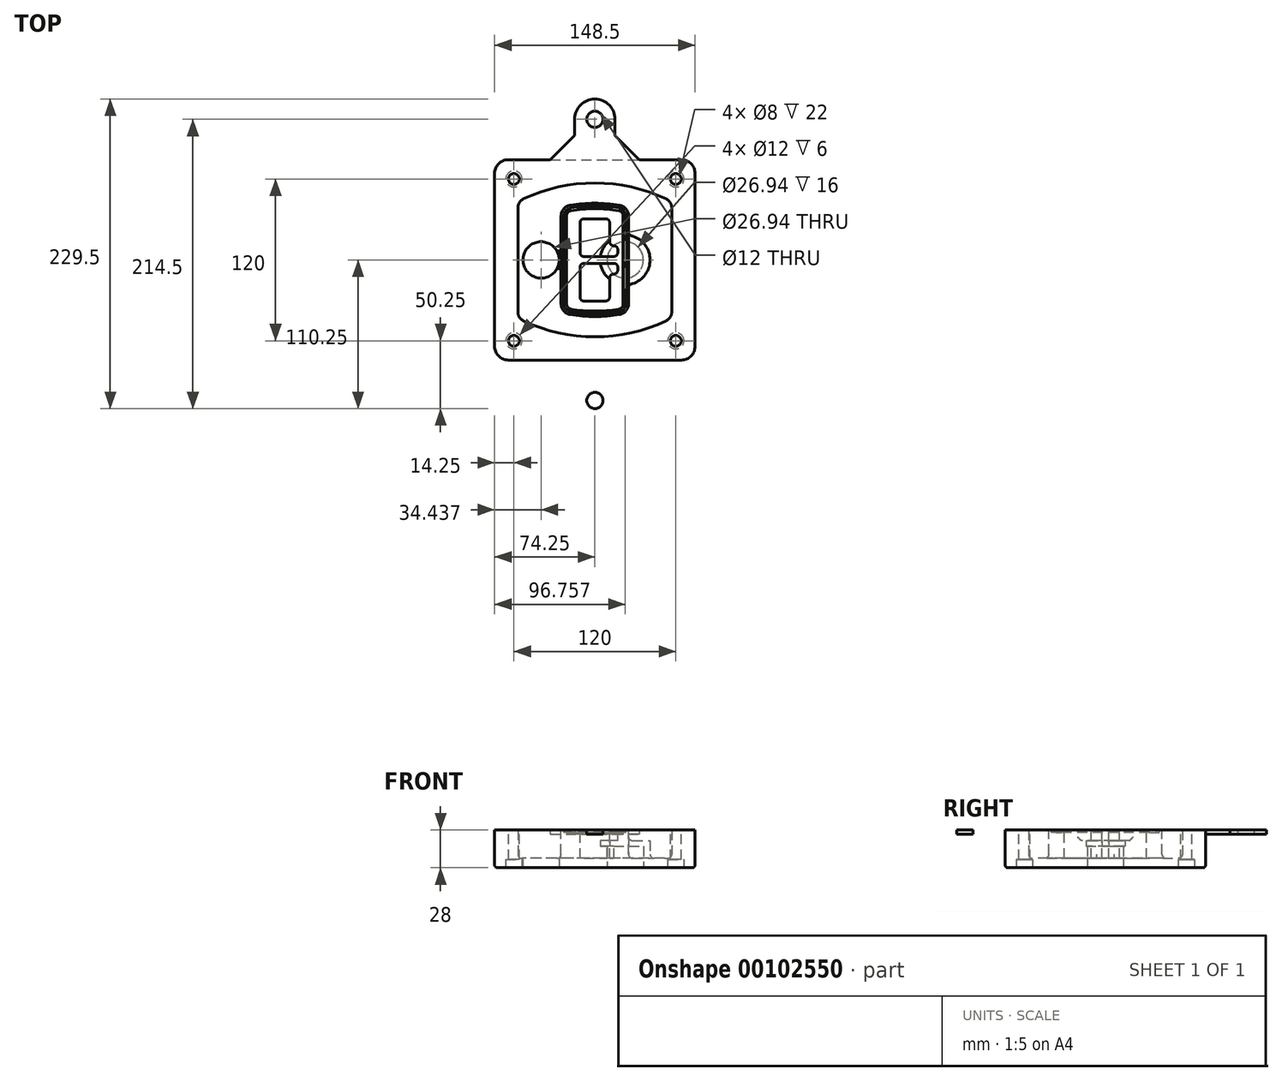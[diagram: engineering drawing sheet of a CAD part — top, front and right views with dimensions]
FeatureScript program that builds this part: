
annotation { "Feature Type Name" : "Feature", "Feature Type Description" : "" }
export const myFeature = defineFeature(function(context is Context, id is Id, definition is map)
    precondition{}
    {
        {
            var Q0;
            Q0=qCreatedBy(makeId("Top.planeOp"),FACE);
            var sketch = newSketch(context, id + "F0", { "sketchPlane" : qUnion([Q0])});
            skPoint(sketch, "E0.rect.middle", {"position": v(0, 0) * mm});
            skLineSegment(sketch, "E1.bottom", {"start": v(-64.25, -74.25) * mm, "end": v(64.25, -74.25) * mm});
            skLineSegment(sketch, "E1.top", {"start": v(-64.25, 74.25) * mm, "end": v(64.25, 74.25) * mm});
            skLineSegment(sketch, "E1.left", {"start": v(-74.25, -64.25) * mm, "end": v(-74.25, 64.25) * mm});
            skLineSegment(sketch, "E1.right", {"start": v(74.25, -64.25) * mm, "end": v(74.25, 64.25) * mm});
            skLineSegment(sketch, "E2", {"start": v(-74.25, 74.25) * mm, "end": v(74.25, -74.25) * mm, "construction": true});
            skLineSegment(sketch, "E3", {"start": v(74.25, 74.25) * mm, "end": v(-74.25, -74.25) * mm, "construction": true});
            skCircle(sketch, "E4", {"center": v(-60, 60) * mm, "radius": 4 * mm});
            skCircle(sketch, "E5", {"center": v(60, 60) * mm, "radius": 4 * mm});
            skCircle(sketch, "E6", {"center": v(60, -60) * mm, "radius": 4 * mm});
            skCircle(sketch, "E7", {"center": v(-60, -60) * mm, "radius": 4 * mm});
            skLineSegment(sketch, "E8", {"start": v(-60, 60) * mm, "end": v(60, 60) * mm, "construction": true});
            skLineSegment(sketch, "E9", {"start": v(60, 60) * mm, "end": v(60, -60) * mm, "construction": true});
            skLineSegment(sketch, "E10", {"start": v(60, -60) * mm, "end": v(-60, -60) * mm, "construction": true});
            skLineSegment(sketch, "E11", {"start": v(-60, -60) * mm, "end": v(-60, 60) * mm, "construction": true});
            skLineSegment(sketch, "E12", {"start": v(-60, 38.83) * mm, "end": v(-60, -38.83) * mm});
            skLineSegment(sketch, "E13", {"start": v(60, 38.83) * mm, "end": v(60, -38.83) * mm});
            skArc(sketch, "E14", {"start": v(54.26, 47.88) * mm, "mid": v(0, 60) * mm, "end": v(-54.26, 47.88) * mm});
            skArc(sketch, "E15", {"start": v(-54.26, -47.88) * mm, "mid": v(0, -60) * mm, "end": v(54.26, -47.88) * mm});
            skLineSegment(sketch, "E16", {"start": v(-60, 0) * mm, "end": v(60, 0) * mm, "construction": true});
            skPoint(sketch, "E17.visualSharp", {"position": v(-60, -45) * mm});
            skArc(sketch, "E17.filletArc", {"start": v(-60, -38.83) * mm, "mid": v(-58.44, -44.2) * mm, "end": v(-54.26, -47.88) * mm});
            skPoint(sketch, "E18.visualSharp", {"position": v(-60, 45) * mm});
            skArc(sketch, "E18.filletArc", {"start": v(-54.26, 47.88) * mm, "mid": v(-58.44, 44.2) * mm, "end": v(-60, 38.83) * mm});
            skPoint(sketch, "E19.visualSharp", {"position": v(60, 45) * mm});
            skArc(sketch, "E19.filletArc", {"start": v(60, 38.83) * mm, "mid": v(58.44, 44.2) * mm, "end": v(54.26, 47.88) * mm});
            skPoint(sketch, "E20.visualSharp", {"position": v(60, -45) * mm});
            skArc(sketch, "E20.filletArc", {"start": v(54.26, -47.88) * mm, "mid": v(58.44, -44.2) * mm, "end": v(60, -38.83) * mm});
            skPoint(sketch, "E21.visualSharp", {"position": v(-74.25, 74.25) * mm});
            skArc(sketch, "E21.filletArc", {"start": v(-64.25, 74.25) * mm, "mid": v(-71.32, 71.32) * mm, "end": v(-74.25, 64.25) * mm});
            skPoint(sketch, "E22.visualSharp", {"position": v(74.25, 74.25) * mm});
            skArc(sketch, "E22.filletArc", {"start": v(74.25, 64.25) * mm, "mid": v(71.32, 71.32) * mm, "end": v(64.25, 74.25) * mm});
            skPoint(sketch, "E23.visualSharp", {"position": v(74.25, -74.25) * mm});
            skArc(sketch, "E23.filletArc", {"start": v(64.25, -74.25) * mm, "mid": v(71.32, -71.32) * mm, "end": v(74.25, -64.25) * mm});
            skPoint(sketch, "E24.visualSharp", {"position": v(-74.25, -74.25) * mm});
            skArc(sketch, "E24.filletArc", {"start": v(-74.25, -64.25) * mm, "mid": v(-71.32, -71.32) * mm, "end": v(-64.25, -74.25) * mm});
            skArc(sketch, "E25.0", {"start": v(57, 38.83) * mm, "mid": v(55.9, 42.58) * mm, "end": v(52.98, 45.17) * mm});
            skLineSegment(sketch, "E25.1", {"start": v(57, 38.83) * mm, "end": v(57, -38.83) * mm});
            skArc(sketch, "E25.2", {"start": v(52.98, -45.17) * mm, "mid": v(55.9, -42.58) * mm, "end": v(57, -38.83) * mm});
            skArc(sketch, "E25.3", {"start": v(-52.98, -45.17) * mm, "mid": v(0, -57) * mm, "end": v(52.98, -45.17) * mm});
            skArc(sketch, "E25.4", {"start": v(-57, -38.83) * mm, "mid": v(-55.9, -42.58) * mm, "end": v(-52.98, -45.17) * mm});
            skArc(sketch, "E25.5", {"start": v(52.98, 45.17) * mm, "mid": v(0, 57) * mm, "end": v(-52.98, 45.17) * mm});
            skLineSegment(sketch, "E25.6", {"start": v(-57, 38.83) * mm, "end": v(-57, -38.83) * mm});
            skArc(sketch, "E25.7", {"start": v(-52.98, 45.17) * mm, "mid": v(-55.9, 42.58) * mm, "end": v(-57, 38.83) * mm});
            skArc(sketch, "E26.0", {"start": v(-55.96, 51.5) * mm, "mid": v(-61.82, 46.33) * mm, "end": v(-64, 38.83) * mm});
            skArc(sketch, "E26.1", {"start": v(55.96, 51.5) * mm, "mid": v(0, 64) * mm, "end": v(-55.96, 51.5) * mm});
            skArc(sketch, "E26.2", {"start": v(64, 38.83) * mm, "mid": v(61.82, 46.33) * mm, "end": v(55.96, 51.5) * mm});
            skLineSegment(sketch, "E26.3", {"start": v(64, 38.83) * mm, "end": v(64, -38.83) * mm});
            skArc(sketch, "E26.4", {"start": v(55.96, -51.5) * mm, "mid": v(61.82, -46.33) * mm, "end": v(64, -38.83) * mm});
            skLineSegment(sketch, "E26.5", {"start": v(-64, 38.83) * mm, "end": v(-64, -38.83) * mm});
            skArc(sketch, "E26.6", {"start": v(-55.96, -51.5) * mm, "mid": v(0, -64) * mm, "end": v(55.96, -51.5) * mm});
            skArc(sketch, "E26.7", {"start": v(-64, -38.83) * mm, "mid": v(-61.82, -46.33) * mm, "end": v(-55.96, -51.5) * mm});
            skSolve(sketch);
        }
        {
            var Q0;
            Q0=makeQuery(id+"F0.imprint","IMPRINT",FACE,{"disambiguationData":[TD([[makeQuery(id+"F0.imprint","IMPRINT",EDGE,{"derivedFrom":sQuery(id+"F0.wireOp",EDGE,"E1.bottom")}),1.0]])]});
            var Q1;
            Q1=makeQuery(id+"F0.imprint","IMPRINT",FACE,{"disambiguationData":[TD([[makeQuery(id+"F0.imprint","IMPRINT",EDGE,{"derivedFrom":sQuery(id+"F0.wireOp",EDGE,"E12")}),1.0]])]});
            var Q2;
            Q2=makeQuery(id+"F0.imprint","IMPRINT",FACE,{"disambiguationData":[TD([[makeQuery(id+"F0.imprint","IMPRINT",EDGE,{"derivedFrom":sQuery(id+"F0.wireOp",EDGE,"E25.0")}),1.0]])]});
            var Q3;
            Q3=makeQuery(id+"F0.imprint","IMPRINT",FACE,{"disambiguationData":[TD([[makeQuery(id+"F0.imprint","IMPRINT",EDGE,{"derivedFrom":sQuery(id+"F0.wireOp",EDGE,"E12")}),-1.0]])]});
            extrude(context, id + "F1", {"entities" : qUnion([Q0, Q1, Q2, Q3]), "oppositeDirection" : true, "depth" : 25 * mm});
        }
        {
            var Q0;
            Q0=makeQuery(id+"F0.imprint","IMPRINT",FACE,{"disambiguationData":[TD([[makeQuery(id+"F0.imprint","IMPRINT",EDGE,{"derivedFrom":sQuery(id+"F0.wireOp",EDGE,"E12")}),1.0]])]});
            extrude(context, id + "F2", {"entities" : qUnion([Q0]), "operationType" : NewBodyOperationType.ADD, "depth" : 3 * mm});
        }
        {
            var Q0;
            Q0=makeQuery(id+"F0.imprint","IMPRINT",FACE,{"disambiguationData":[TD([[makeQuery(id+"F0.imprint","IMPRINT",EDGE,{"derivedFrom":sQuery(id+"F0.wireOp",EDGE,"E25.0")}),1.0]])]});
            extrude(context, id + "F3", {"entities" : qUnion([Q0]), "operationType" : NewBodyOperationType.REMOVE, "oppositeDirection" : true, "depth" : 18 * mm});
        }
        {
            var Q0;
            Q0=makeQuery(id+"F2.opExtrude","CAP_FACE",FACE,{"disambiguationData":[OSD([sQuery(id+"F0.wireOp",EDGE,"E12"),sQuery(id+"F0.wireOp",EDGE,"E13"),sQuery(id+"F0.wireOp",EDGE,"E14"),sQuery(id+"F0.wireOp",EDGE,"E15"),sQuery(id+"F0.wireOp",EDGE,"E17.filletArc"),sQuery(id+"F0.wireOp",EDGE,"E18.filletArc"),sQuery(id+"F0.wireOp",EDGE,"E19.filletArc"),sQuery(id+"F0.wireOp",EDGE,"E20.filletArc"),sQuery(id+"F0.wireOp",EDGE,"E25.0"),sQuery(id+"F0.wireOp",EDGE,"E25.1"),sQuery(id+"F0.wireOp",EDGE,"E25.2"),sQuery(id+"F0.wireOp",EDGE,"E25.3"),sQuery(id+"F0.wireOp",EDGE,"E25.4"),sQuery(id+"F0.wireOp",EDGE,"E25.5"),sQuery(id+"F0.wireOp",EDGE,"E25.6"),sQuery(id+"F0.wireOp",EDGE,"E25.7")])],"isStart":false});
            var sketch = newSketch(context, id + "F4", { "sketchPlane" : qUnion([Q0])});
            skArc(sketch, "E27.0", {"start": v(-18.34, -40.45) * mm, "mid": v(0, -42) * mm, "end": v(18.34, -40.45) * mm});
            skArc(sketch, "E28.0", {"start": v(18.34, 40.45) * mm, "mid": v(0, 42) * mm, "end": v(-18.34, 40.45) * mm});
            skLineSegment(sketch, "E29", {"start": v(-25, 32.57) * mm, "end": v(-25, -32.57) * mm});
            skLineSegment(sketch, "E30", {"start": v(25, 32.57) * mm, "end": v(25, -32.57) * mm});
            skLineSegment(sketch, "E31", {"start": v(-25, 39.1) * mm, "end": v(25, 39.1) * mm, "construction": true});
            skLineSegment(sketch, "E32", {"start": v(-25, -39.1) * mm, "end": v(25, -39.1) * mm, "construction": true});
            skPoint(sketch, "E33.visualSharp", {"position": v(-25, 39.1) * mm});
            skArc(sketch, "E33.filletArc", {"start": v(-18.34, 40.45) * mm, "mid": v(-23.11, 37.73) * mm, "end": v(-25, 32.57) * mm});
            skPoint(sketch, "E34.visualSharp", {"position": v(25, 39.1) * mm});
            skArc(sketch, "E34.filletArc", {"start": v(25, 32.57) * mm, "mid": v(23.11, 37.73) * mm, "end": v(18.34, 40.45) * mm});
            skPoint(sketch, "E35.visualSharp", {"position": v(25, -39.1) * mm});
            skArc(sketch, "E35.filletArc", {"start": v(18.34, -40.45) * mm, "mid": v(23.11, -37.73) * mm, "end": v(25, -32.57) * mm});
            skPoint(sketch, "E36.visualSharp", {"position": v(-25, -39.1) * mm});
            skArc(sketch, "E36.filletArc", {"start": v(-25, -32.57) * mm, "mid": v(-23.11, -37.73) * mm, "end": v(-18.34, -40.45) * mm});
            skArc(sketch, "E37.0", {"start": v(52.98, 45.17) * mm, "mid": v(0, 57) * mm, "end": v(-52.98, 45.17) * mm});
            skArc(sketch, "E37.1", {"start": v(-52.98, 45.17) * mm, "mid": v(-55.9, 42.58) * mm, "end": v(-57, 38.83) * mm});
            skLineSegment(sketch, "E37.2", {"start": v(-57, 38.83) * mm, "end": v(-57, -38.83) * mm});
            skArc(sketch, "E37.3", {"start": v(-57, -38.83) * mm, "mid": v(-55.9, -42.58) * mm, "end": v(-52.98, -45.17) * mm});
            skArc(sketch, "E37.4", {"start": v(-52.98, -45.17) * mm, "mid": v(0, -57) * mm, "end": v(52.98, -45.17) * mm});
            skArc(sketch, "E37.5", {"start": v(52.98, -45.17) * mm, "mid": v(55.9, -42.58) * mm, "end": v(57, -38.83) * mm});
            skLineSegment(sketch, "E37.6", {"start": v(57, 38.83) * mm, "end": v(57, -38.83) * mm});
            skArc(sketch, "E37.7", {"start": v(57, 38.83) * mm, "mid": v(55.9, 42.58) * mm, "end": v(52.98, 45.17) * mm});
            skLineSegment(sketch, "E38.0", {"start": v(23, 32.57) * mm, "end": v(23, -32.57) * mm});
            skArc(sketch, "E38.1", {"start": v(18, -38.48) * mm, "mid": v(21.58, -36.44) * mm, "end": v(23, -32.57) * mm});
            skArc(sketch, "E38.2", {"start": v(-18, -38.48) * mm, "mid": v(0, -40) * mm, "end": v(18, -38.48) * mm});
            skArc(sketch, "E38.3", {"start": v(-23, -32.57) * mm, "mid": v(-21.58, -36.44) * mm, "end": v(-18, -38.48) * mm});
            skLineSegment(sketch, "E38.4", {"start": v(-23, 32.57) * mm, "end": v(-23, -32.57) * mm});
            skArc(sketch, "E38.5", {"start": v(23, 32.57) * mm, "mid": v(21.58, 36.44) * mm, "end": v(18, 38.48) * mm});
            skArc(sketch, "E38.6", {"start": v(-18, 38.48) * mm, "mid": v(-21.58, 36.44) * mm, "end": v(-23, 32.57) * mm});
            skArc(sketch, "E38.7", {"start": v(18, 38.48) * mm, "mid": v(0, 40) * mm, "end": v(-18, 38.48) * mm});
            skArc(sketch, "E39.0", {"start": v(21, 32.57) * mm, "mid": v(20.06, 35.15) * mm, "end": v(17.67, 36.5) * mm});
            skLineSegment(sketch, "E39.1", {"start": v(21, 32.57) * mm, "end": v(21, -32.57) * mm});
            skArc(sketch, "E39.2", {"start": v(17.67, -36.5) * mm, "mid": v(20.06, -35.15) * mm, "end": v(21, -32.57) * mm});
            skArc(sketch, "E39.3", {"start": v(-17.67, -36.5) * mm, "mid": v(0, -38) * mm, "end": v(17.67, -36.5) * mm});
            skArc(sketch, "E39.4", {"start": v(-21, -32.57) * mm, "mid": v(-20.06, -35.15) * mm, "end": v(-17.67, -36.5) * mm});
            skArc(sketch, "E39.5", {"start": v(17.67, 36.5) * mm, "mid": v(0, 38) * mm, "end": v(-17.67, 36.5) * mm});
            skLineSegment(sketch, "E39.6", {"start": v(-21, 32.57) * mm, "end": v(-21, -32.57) * mm});
            skArc(sketch, "E39.7", {"start": v(-17.67, 36.5) * mm, "mid": v(-20.06, 35.15) * mm, "end": v(-21, 32.57) * mm});
            skLineSegment(sketch, "E40", {"start": v(-25, 0) * mm, "end": v(25, 0) * mm, "construction": true});
            skLineSegment(sketch, "E41", {"start": v(-11, 5.5) * mm, "end": v(-11, 27.5) * mm});
            skLineSegment(sketch, "E42", {"start": v(-8, 30.5) * mm, "end": v(8, 30.5) * mm});
            skLineSegment(sketch, "E43", {"start": v(11, 27.5) * mm, "end": v(11, 13.5) * mm});
            skLineSegment(sketch, "E44", {"start": v(14, 10.5) * mm, "end": v(14, 10.5) * mm});
            skLineSegment(sketch, "E45", {"start": v(17, 7.5) * mm, "end": v(17, 5.5) * mm});
            skLineSegment(sketch, "E46", {"start": v(14, 2.5) * mm, "end": v(-8, 2.5) * mm});
            skPoint(sketch, "E47.visualSharp", {"position": v(-11, 30.5) * mm});
            skArc(sketch, "E47.filletArc", {"start": v(-8, 30.5) * mm, "mid": v(-10.12, 29.62) * mm, "end": v(-11, 27.5) * mm});
            skPoint(sketch, "E48.visualSharp", {"position": v(11, 30.5) * mm});
            skArc(sketch, "E48.filletArc", {"start": v(11, 27.5) * mm, "mid": v(10.12, 29.62) * mm, "end": v(8, 30.5) * mm});
            skPoint(sketch, "E49.visualSharp", {"position": v(11, 10.5) * mm});
            skArc(sketch, "E49.filletArc", {"start": v(11, 13.5) * mm, "mid": v(11.88, 11.38) * mm, "end": v(14, 10.5) * mm});
            skPoint(sketch, "E50.visualSharp", {"position": v(17, 10.5) * mm});
            skArc(sketch, "E50.filletArc", {"start": v(17, 7.5) * mm, "mid": v(16.12, 9.62) * mm, "end": v(14, 10.5) * mm});
            skPoint(sketch, "E51.visualSharp", {"position": v(17, 2.5) * mm});
            skArc(sketch, "E51.filletArc", {"start": v(14, 2.5) * mm, "mid": v(16.12, 3.38) * mm, "end": v(17, 5.5) * mm});
            skPoint(sketch, "E52.visualSharp", {"position": v(-11, 2.5) * mm});
            skArc(sketch, "E52.filletArc", {"start": v(-11, 5.5) * mm, "mid": v(-10.12, 3.38) * mm, "end": v(-8, 2.5) * mm});
            skLineSegment(sketch, "E53.0.MirrorCS", {"start": v(14, -2.5) * mm, "end": v(-8, -2.5) * mm});
            skArc(sketch, "E54.0.MirrorCS", {"start": v(-11, -5.5) * mm, "mid": v(-10.12, -3.38) * mm, "end": v(-8, -2.5) * mm});
            skLineSegment(sketch, "E55.0.MirrorCS", {"start": v(-11, -5.5) * mm, "end": v(-11, -27.5) * mm});
            skArc(sketch, "E56.0.MirrorCS", {"start": v(-8, -30.5) * mm, "mid": v(-10.12, -29.62) * mm, "end": v(-11, -27.5) * mm});
            skLineSegment(sketch, "E57.0.MirrorCS", {"start": v(-8, -30.5) * mm, "end": v(8, -30.5) * mm});
            skArc(sketch, "E58.0.MirrorCS", {"start": v(11, -27.5) * mm, "mid": v(10.12, -29.62) * mm, "end": v(8, -30.5) * mm});
            skLineSegment(sketch, "E59.0.MirrorCS", {"start": v(11, -27.5) * mm, "end": v(11, -13.5) * mm});
            skArc(sketch, "E60.0.MirrorCS", {"start": v(11, -13.5) * mm, "mid": v(11.88, -11.38) * mm, "end": v(14, -10.5) * mm});
            skArc(sketch, "E61.0.MirrorCS", {"start": v(17, -7.5) * mm, "mid": v(16.12, -9.62) * mm, "end": v(14, -10.5) * mm});
            skLineSegment(sketch, "E62.0.MirrorCS", {"start": v(17, -7.5) * mm, "end": v(17, -5.5) * mm});
            skArc(sketch, "E63.0.MirrorCS", {"start": v(14, -2.5) * mm, "mid": v(16.12, -3.38) * mm, "end": v(17, -5.5) * mm});
            skSolve(sketch);
        }
        {
            var Q0;
            Q0=makeQuery(id+"F4.imprint","IMPRINT",FACE,{"disambiguationData":[TD([[makeQuery(id+"F4.imprint","IMPRINT",EDGE,{"derivedFrom":sQuery(id+"F4.wireOp",EDGE,"E27.0")}),1.0]])]});
            var Q1;
            Q1=makeQuery(id+"F4.imprint","IMPRINT",FACE,{"disambiguationData":[TD([[makeQuery(id+"F4.imprint","IMPRINT",EDGE,{"derivedFrom":sQuery(id+"F4.wireOp",EDGE,"E38.0")}),-1.0]])]});
            var Q2;
            Q2=makeQuery(id+"F4.imprint","IMPRINT",FACE,{"disambiguationData":[TD([[makeQuery(id+"F4.imprint","IMPRINT",EDGE,{"derivedFrom":sQuery(id+"F4.wireOp",EDGE,"E39.0")}),1.0]])]});
            extrude(context, id + "F5", {"entities" : qUnion([Q0, Q1, Q2]), "operationType" : NewBodyOperationType.ADD, "endBound" : BoundingType.UP_TO_NEXT, "oppositeDirection" : true, "depth" : 25 * mm});
        }
        {
            var Q0;
            Q0=makeQuery(id+"F4.imprint","IMPRINT",FACE,{"disambiguationData":[TD([[makeQuery(id+"F4.imprint","IMPRINT",EDGE,{"derivedFrom":sQuery(id+"F4.wireOp",EDGE,"E38.0")}),-1.0]])]});
            extrude(context, id + "F6", {"entities" : qUnion([Q0]), "operationType" : NewBodyOperationType.REMOVE, "oppositeDirection" : true, "depth" : 2 * mm});
        }
        {
            var Q0;
            Q0=makeQuery(id+"F1.opExtrude","CAP_FACE",FACE,{"disambiguationData":[OSD([sQuery(id+"F0.wireOp",EDGE,"E1.bottom"),sQuery(id+"F0.wireOp",EDGE,"E1.top"),sQuery(id+"F0.wireOp",EDGE,"E1.left"),sQuery(id+"F0.wireOp",EDGE,"E1.right"),sQuery(id+"F0.wireOp",EDGE,"E4"),sQuery(id+"F0.wireOp",EDGE,"E5"),sQuery(id+"F0.wireOp",EDGE,"E6"),sQuery(id+"F0.wireOp",EDGE,"E7"),sQuery(id+"F0.wireOp",EDGE,"E21.filletArc"),sQuery(id+"F0.wireOp",EDGE,"E22.filletArc"),sQuery(id+"F0.wireOp",EDGE,"E23.filletArc"),sQuery(id+"F0.wireOp",EDGE,"E24.filletArc")])],"isStart":false});
            var sketch = newSketch(context, id + "F7", { "sketchPlane" : qUnion([Q0])});
            skCircle(sketch, "E64", {"center": v(22.5, 0) * mm, "radius": 13.47 * mm});
            skCircle(sketch, "E65", {"center": v(-39.81, 0) * mm, "radius": 13.47 * mm});
            skLineSegment(sketch, "E66", {"start": v(74.25, 0) * mm, "end": v(-74.25, 0) * mm});
            skCircle(sketch, "E67", {"center": v(22.5, 0) * mm, "radius": 18.47 * mm});
            skCircle(sketch, "E68", {"center": v(60, -60) * mm, "radius": 6 * mm});
            skCircle(sketch, "E69", {"center": v(-60, -60) * mm, "radius": 6 * mm});
            skCircle(sketch, "E70", {"center": v(-60, 60) * mm, "radius": 6 * mm});
            skCircle(sketch, "E71", {"center": v(60, 60) * mm, "radius": 6 * mm});
            skSolve(sketch);
        }
        {
            var Q0;
            {var subQ1=sQuery(id+"F7.wireOp",EDGE,"E66");var subQ4=sQuery(id+"F7.wireOp",EDGE,"E64");var subQ6=makeQuery(id+"F7.imprint","INTERSECT",VERTEX,{"disambiguationData":[OD(0.0)],"derivedFrom":[subQ4,subQ1]});Q0=makeQuery(id+"F7.imprint","IMPRINT",FACE,{"disambiguationData":[TD([[makeQuery(id+"F7.imprint","IMPRINT",EDGE,{"disambiguationData":[TD([[subQ6,-1.0]])],"derivedFrom":subQ4}),-1.0]])]});}
            var Q1;
            {var subQ0=sQuery(id+"F7.wireOp",EDGE,"E66");var subQ1=sQuery(id+"F7.wireOp",EDGE,"E64");var subQ3=makeQuery(id+"F7.imprint","INTERSECT",VERTEX,{"disambiguationData":[OD(0.0)],"derivedFrom":[subQ1,subQ0]});Q1=makeQuery(id+"F7.imprint","IMPRINT",FACE,{"disambiguationData":[TD([[makeQuery(id+"F7.imprint","IMPRINT",EDGE,{"disambiguationData":[TD([[subQ3,-1.0]])],"derivedFrom":subQ1}),1.0]])]});}
            var Q2;
            {var subQ0=sQuery(id+"F7.wireOp",EDGE,"E66");var subQ1=sQuery(id+"F7.wireOp",EDGE,"E64");var subQ3=makeQuery(id+"F7.imprint","INTERSECT",VERTEX,{"disambiguationData":[OD(0.0)],"derivedFrom":[subQ1,subQ0]});Q2=makeQuery(id+"F7.imprint","IMPRINT",FACE,{"disambiguationData":[TD([[makeQuery(id+"F7.imprint","IMPRINT",EDGE,{"disambiguationData":[TD([[subQ3,1.0]])],"derivedFrom":subQ1}),1.0]])]});}
            var Q3;
            {var subQ1=sQuery(id+"F7.wireOp",EDGE,"E66");var subQ4=sQuery(id+"F7.wireOp",EDGE,"E64");var subQ6=makeQuery(id+"F7.imprint","INTERSECT",VERTEX,{"disambiguationData":[OD(0.0)],"derivedFrom":[subQ4,subQ1]});Q3=makeQuery(id+"F7.imprint","IMPRINT",FACE,{"disambiguationData":[TD([[makeQuery(id+"F7.imprint","IMPRINT",EDGE,{"disambiguationData":[TD([[subQ6,1.0]])],"derivedFrom":subQ4}),-1.0]])]});}
            extrude(context, id + "F8", {"entities" : qUnion([Q0, Q1, Q2, Q3]), "operationType" : NewBodyOperationType.ADD, "oppositeDirection" : true, "depth" : 20 * mm});
        }
        {
            var Q0;
            {var subQ0=sQuery(id+"F7.wireOp",EDGE,"E66");var subQ1=sQuery(id+"F7.wireOp",EDGE,"E64");var subQ3=makeQuery(id+"F7.imprint","INTERSECT",VERTEX,{"disambiguationData":[OD(0.0)],"derivedFrom":[subQ1,subQ0]});Q0=makeQuery(id+"F7.imprint","IMPRINT",FACE,{"disambiguationData":[TD([[makeQuery(id+"F7.imprint","IMPRINT",EDGE,{"disambiguationData":[TD([[subQ3,-1.0]])],"derivedFrom":subQ1}),1.0]])]});}
            var Q1;
            {var subQ0=sQuery(id+"F7.wireOp",EDGE,"E66");var subQ1=sQuery(id+"F7.wireOp",EDGE,"E64");var subQ3=makeQuery(id+"F7.imprint","INTERSECT",VERTEX,{"disambiguationData":[OD(0.0)],"derivedFrom":[subQ1,subQ0]});Q1=makeQuery(id+"F7.imprint","IMPRINT",FACE,{"disambiguationData":[TD([[makeQuery(id+"F7.imprint","IMPRINT",EDGE,{"disambiguationData":[TD([[subQ3,1.0]])],"derivedFrom":subQ1}),1.0]])]});}
            extrude(context, id + "F9", {"entities" : qUnion([Q0, Q1]), "operationType" : NewBodyOperationType.REMOVE, "oppositeDirection" : true, "depth" : 16 * mm});
        }
        {
            var Q0;
            {var subQ0=sQuery(id+"F7.wireOp",EDGE,"E66");var subQ1=sQuery(id+"F7.wireOp",EDGE,"E65");var subQ3=makeQuery(id+"F7.imprint","INTERSECT",VERTEX,{"disambiguationData":[OD(0.0)],"derivedFrom":[subQ1,subQ0]});Q0=makeQuery(id+"F7.imprint","IMPRINT",FACE,{"disambiguationData":[TD([[makeQuery(id+"F7.imprint","IMPRINT",EDGE,{"disambiguationData":[TD([[subQ3,-1.0]])],"derivedFrom":subQ1}),1.0]])]});}
            var Q1;
            {var subQ0=sQuery(id+"F7.wireOp",EDGE,"E66");var subQ1=sQuery(id+"F7.wireOp",EDGE,"E65");var subQ3=makeQuery(id+"F7.imprint","INTERSECT",VERTEX,{"disambiguationData":[OD(0.0)],"derivedFrom":[subQ1,subQ0]});Q1=makeQuery(id+"F7.imprint","IMPRINT",FACE,{"disambiguationData":[TD([[makeQuery(id+"F7.imprint","IMPRINT",EDGE,{"disambiguationData":[TD([[subQ3,1.0]])],"derivedFrom":subQ1}),1.0]])]});}
            extrude(context, id + "F10", {"entities" : qUnion([Q0, Q1]), "operationType" : NewBodyOperationType.REMOVE, "oppositeDirection" : true, "depth" : 25 * mm});
        }
        {
            var Q0;
            Q0=makeQuery(id+"F7.imprint","IMPRINT",FACE,{"disambiguationData":[TD([[makeQuery(id+"F7.imprint","IMPRINT",EDGE,{"derivedFrom":sQuery(id+"F7.wireOp",EDGE,"E68")}),1.0]])]});
            var Q1;
            Q1=makeQuery(id+"F7.imprint","IMPRINT",FACE,{"disambiguationData":[TD([[makeQuery(id+"F7.imprint","IMPRINT",EDGE,{"derivedFrom":makeQuery(id+"F1.opExtrude","CAP_EDGE",EDGE,{"disambiguationData":[OSD([sQuery(id+"F0.wireOp",EDGE,"E5")])],"isStart":false})}),-1.0]])]});
            var Q2;
            Q2=makeQuery(id+"F7.imprint","IMPRINT",FACE,{"disambiguationData":[TD([[makeQuery(id+"F7.imprint","IMPRINT",EDGE,{"derivedFrom":sQuery(id+"F7.wireOp",EDGE,"E69")}),1.0]])]});
            var Q3;
            Q3=makeQuery(id+"F7.imprint","IMPRINT",FACE,{"disambiguationData":[TD([[makeQuery(id+"F7.imprint","IMPRINT",EDGE,{"derivedFrom":makeQuery(id+"F1.opExtrude","CAP_EDGE",EDGE,{"disambiguationData":[OSD([sQuery(id+"F0.wireOp",EDGE,"E4")])],"isStart":false})}),-1.0]])]});
            var Q4;
            Q4=makeQuery(id+"F7.imprint","IMPRINT",FACE,{"disambiguationData":[TD([[makeQuery(id+"F7.imprint","IMPRINT",EDGE,{"derivedFrom":sQuery(id+"F7.wireOp",EDGE,"E70")}),1.0]])]});
            var Q5;
            Q5=makeQuery(id+"F7.imprint","IMPRINT",FACE,{"disambiguationData":[TD([[makeQuery(id+"F7.imprint","IMPRINT",EDGE,{"derivedFrom":makeQuery(id+"F1.opExtrude","CAP_EDGE",EDGE,{"disambiguationData":[OSD([sQuery(id+"F0.wireOp",EDGE,"E7")])],"isStart":false})}),-1.0]])]});
            var Q6;
            Q6=makeQuery(id+"F7.imprint","IMPRINT",FACE,{"disambiguationData":[TD([[makeQuery(id+"F7.imprint","IMPRINT",EDGE,{"derivedFrom":sQuery(id+"F7.wireOp",EDGE,"E71")}),1.0]])]});
            var Q7;
            Q7=makeQuery(id+"F7.imprint","IMPRINT",FACE,{"disambiguationData":[TD([[makeQuery(id+"F7.imprint","IMPRINT",EDGE,{"derivedFrom":makeQuery(id+"F1.opExtrude","CAP_EDGE",EDGE,{"disambiguationData":[OSD([sQuery(id+"F0.wireOp",EDGE,"E6")])],"isStart":false})}),-1.0]])]});
            extrude(context, id + "F11", {"entities" : qUnion([Q0, Q1, Q2, Q3, Q4, Q5, Q6, Q7]), "operationType" : NewBodyOperationType.REMOVE, "oppositeDirection" : true, "depth" : 6 * mm});
        }
        {
            var Q0;
            Q0=makeQuery(id+"F9.boolean.opBoolean","COPY",FACE,{"derivedFrom":makeQuery(id+"F9.opExtrude","CAP_FACE",FACE,{"disambiguationData":[OSD([sQuery(id+"F7.wireOp",EDGE,"E64")])],"isStart":false})});
            var sketch = newSketch(context, id + "F12", { "sketchPlane" : qUnion([Q0])});
            skArc(sketch, "E72.0", {"start": v(11, 14.45) * mm, "mid": v(6.45, 9.13) * mm, "end": v(4.2, 2.5) * mm});
            skArc(sketch, "E72.1", {"start": v(4.2, -2.5) * mm, "mid": v(6.45, -9.13) * mm, "end": v(11, -14.45) * mm});
            skLineSegment(sketch, "E73", {"start": v(4.2, -2.5) * mm, "end": v(14, -2.5) * mm});
            skLineSegment(sketch, "E74.0", {"start": v(14, 2.5) * mm, "end": v(4.2, 2.5) * mm});
            skArc(sketch, "E74.1", {"start": v(14, 2.5) * mm, "mid": v(16.12, 3.38) * mm, "end": v(17, 5.5) * mm});
            skLineSegment(sketch, "E74.2", {"start": v(17, 7.5) * mm, "end": v(17, 5.5) * mm});
            skArc(sketch, "E74.3", {"start": v(17, 7.5) * mm, "mid": v(16.12, 9.62) * mm, "end": v(14, 10.5) * mm});
            skArc(sketch, "E74.4", {"start": v(11, 13.5) * mm, "mid": v(11.88, 11.38) * mm, "end": v(14, 10.5) * mm});
            skLineSegment(sketch, "E74.5", {"start": v(11, 14.45) * mm, "end": v(11, 13.5) * mm});
            skLineSegment(sketch, "E74.7", {"start": v(14, -2.5) * mm, "end": v(4.2, -2.5) * mm});
            skArc(sketch, "E74.8", {"start": v(14, -2.5) * mm, "mid": v(16.12, -3.38) * mm, "end": v(17, -5.5) * mm});
            skLineSegment(sketch, "E74.9", {"start": v(17, -7.5) * mm, "end": v(17, -5.5) * mm});
            skArc(sketch, "E74.10", {"start": v(17, -7.5) * mm, "mid": v(16.12, -9.62) * mm, "end": v(14, -10.5) * mm});
            skArc(sketch, "E74.11", {"start": v(11, -13.5) * mm, "mid": v(11.88, -11.38) * mm, "end": v(14, -10.5) * mm});
            skLineSegment(sketch, "E74.12", {"start": v(11, -14.45) * mm, "end": v(11, -13.5) * mm});
            skPoint(sketch, "E75.orphan", {"position": v(11, -27.5) * mm});
            skPoint(sketch, "E76.orphan", {"position": v(-8, -2.5) * mm});
            skPoint(sketch, "E77.orphan", {"position": v(-8, 2.5) * mm});
            skPoint(sketch, "E78.orphan", {"position": v(11, 27.5) * mm});
            skSolve(sketch);
        }
        {
            var Q0;
            {var subQ7=sQuery(id+"F12.wireOp",EDGE,"E72.0");var subQ14=sQuery(id+"F12.wireOp",EDGE,"E72.1");var subQ16=sQuery(id+"F12.wireOp",EDGE,"E74.1");var subQ18=sQuery(id+"F12.wireOp",EDGE,"E74.8");Q0=qUnion([makeQuery(id+"F12.imprint","IMPRINT",FACE,{"disambiguationData":[TD([[makeQuery(id+"F12.imprint","IMPRINT",EDGE,{"derivedFrom":subQ7}),1.0]])]}),makeQuery(id+"F12.imprint","IMPRINT",FACE,{"disambiguationData":[TD([[makeQuery(id+"F12.imprint","IMPRINT",EDGE,{"derivedFrom":subQ14}),1.0]])]}),makeQuery(id+"F12.imprint","IMPRINT",FACE,{"disambiguationData":[TD([[makeQuery(id+"F12.imprint","IMPRINT",EDGE,{"derivedFrom":subQ16}),1.0]])]}),makeQuery(id+"F12.imprint","IMPRINT",FACE,{"disambiguationData":[TD([[makeQuery(id+"F12.imprint","IMPRINT",EDGE,{"derivedFrom":subQ18}),-1.0]])]})]);}
            var Q1;
            Q1=makeQuery(id+"F5.boolean.opBoolean","SPLIT",FACE,{"disambiguationData":[TD([makeQuery(id+"F5.opExtrude","SWEPT_FACE",FACE,{"disambiguationData":[OSD([sQuery(id+"F4.wireOp",EDGE,"E41")])]})])],"derivedFrom":makeQuery(id+"F3.boolean.opBoolean","COPY",FACE,{"derivedFrom":makeQuery(id+"F3.opExtrude","CAP_FACE",FACE,{"disambiguationData":[OSD([sQuery(id+"F0.wireOp",EDGE,"E25.0"),sQuery(id+"F0.wireOp",EDGE,"E25.1"),sQuery(id+"F0.wireOp",EDGE,"E25.2"),sQuery(id+"F0.wireOp",EDGE,"E25.3"),sQuery(id+"F0.wireOp",EDGE,"E25.4"),sQuery(id+"F0.wireOp",EDGE,"E25.5"),sQuery(id+"F0.wireOp",EDGE,"E25.6"),sQuery(id+"F0.wireOp",EDGE,"E25.7")])],"isStart":false})})});
            extrude(context, id + "F13", {"entities" : qUnion([Q0]), "operationType" : NewBodyOperationType.REMOVE, "endBound" : BoundingType.UP_TO_SURFACE, "endBoundEntityFace" : qUnion([Q1]), "depth" : 25 * mm});
        }
        {
            var Q0;
            Q0=makeQuery(id+"F3.boolean.opBoolean","COPY",EDGE,{"derivedFrom":makeQuery(id+"F3.opExtrude","CAP_EDGE",EDGE,{"disambiguationData":[OSD([sQuery(id+"F0.wireOp",EDGE,"E25.6")])],"isStart":false})});
            var Q1;
            Q1=makeQuery(id+"F8.boolean.opBoolean","INTERSECT",EDGE,{"derivedFrom":[makeQuery(id+"F5.opExtrude","SWEPT_FACE",FACE,{"disambiguationData":[OSD([sQuery(id+"F4.wireOp",EDGE,"E30")])]}),makeQuery(id+"F8.opExtrude","CAP_FACE",FACE,{"disambiguationData":[OSD([sQuery(id+"F7.wireOp",EDGE,"E67")])],"isStart":false})]});
            var Q2;
            Q2=makeQuery(id+"F8.boolean.opBoolean","INTERSECT",EDGE,{"disambiguationData":[OD(1.0)],"derivedFrom":[makeQuery(id+"F5.opExtrude","SWEPT_FACE",FACE,{"disambiguationData":[OSD([sQuery(id+"F4.wireOp",EDGE,"E30")])]}),makeQuery(id+"F8.opExtrude","SWEPT_FACE",FACE,{"disambiguationData":[OSD([sQuery(id+"F7.wireOp",EDGE,"E67")])]})]});
            var Q3;
            {var subQ0=sQuery(id+"F4.wireOp",EDGE,"E30");Q3=makeQuery(id+"F8.boolean.opBoolean","SPLIT",EDGE,{"disambiguationData":[TD([makeQuery(id+"F5.opExtrude","SWEPT_FACE",FACE,{"disambiguationData":[OSD([sQuery(id+"F4.wireOp",EDGE,"E35.filletArc")])]})])],"derivedFrom":makeQuery(id+"F5.opExtrude","CAP_EDGE",EDGE,{"disambiguationData":[OSD([subQ0])],"isStart":false})});}
            var Q4;
            {var subQ0=sQuery(id+"F0.wireOp",EDGE,"E25.7");var subQ1=sQuery(id+"F0.wireOp",EDGE,"E25.1");var subQ2=sQuery(id+"F0.wireOp",EDGE,"E25.6");var subQ3=sQuery(id+"F0.wireOp",EDGE,"E25.5");var subQ4=sQuery(id+"F0.wireOp",EDGE,"E25.4");var subQ5=sQuery(id+"F0.wireOp",EDGE,"E25.0");var subQ6=sQuery(id+"F0.wireOp",EDGE,"E25.2");var subQ7=sQuery(id+"F0.wireOp",EDGE,"E25.3");Q4=makeQuery(id+"F8.boolean.opBoolean","INTERSECT",EDGE,{"derivedFrom":[makeQuery(id+"F5.boolean.opBoolean","SPLIT",FACE,{"disambiguationData":[TD([makeQuery(id+"F2.opExtrude","SWEPT_FACE",FACE,{"disambiguationData":[OSD([subQ5])]})])],"derivedFrom":makeQuery(id+"F3.boolean.opBoolean","COPY",FACE,{"derivedFrom":makeQuery(id+"F3.opExtrude","CAP_FACE",FACE,{"disambiguationData":[OSD([subQ5,subQ1,subQ6,subQ7,subQ4,subQ3,subQ2,subQ0])],"isStart":false})})}),makeQuery(id+"F8.opExtrude","SWEPT_FACE",FACE,{"disambiguationData":[OSD([sQuery(id+"F7.wireOp",EDGE,"E67")])]})]});}
            var Q5;
            Q5=makeQuery(id+"F8.boolean.opBoolean","INTERSECT",EDGE,{"disambiguationData":[OD(0.0)],"derivedFrom":[makeQuery(id+"F5.opExtrude","SWEPT_FACE",FACE,{"disambiguationData":[OSD([sQuery(id+"F4.wireOp",EDGE,"E30")])]}),makeQuery(id+"F8.opExtrude","SWEPT_FACE",FACE,{"disambiguationData":[OSD([sQuery(id+"F7.wireOp",EDGE,"E67")])]})]});
            fillet(context, id + "F14", {"entities" : qUnion([Q0, Q1, Q2, Q3, Q4, Q5]), "radius" : 3 * mm, "tangentPropagation" : true, "allowEdgeOverflow" : false});
        }
        {
            var Q0;
            Q0=makeQuery(id+"F1.opExtrude","CAP_EDGE",EDGE,{"disambiguationData":[OSD([sQuery(id+"F0.wireOp",EDGE,"E1.bottom")])],"isStart":false});
            fillet(context, id + "F15", {"entities" : qUnion([Q0]), "radius" : 2 * mm, "tangentPropagation" : true, "allowEdgeOverflow" : false});
        }
        {
            var Q0;
            {var subQ0=sQuery(id+"F0.wireOp",EDGE,"E22.filletArc");var subQ1=sQuery(id+"F0.wireOp",EDGE,"E7");var subQ2=sQuery(id+"F0.wireOp",EDGE,"E6");var subQ3=sQuery(id+"F0.wireOp",EDGE,"E5");var subQ4=sQuery(id+"F0.wireOp",EDGE,"E4");var subQ5=sQuery(id+"F0.wireOp",EDGE,"E1.bottom");var subQ6=sQuery(id+"F0.wireOp",EDGE,"E21.filletArc");var subQ7=sQuery(id+"F0.wireOp",EDGE,"E1.top");var subQ8=sQuery(id+"F0.wireOp",EDGE,"E1.left");var subQ9=sQuery(id+"F0.wireOp",EDGE,"E1.right");var subQ10=sQuery(id+"F0.wireOp",EDGE,"E23.filletArc");var subQ11=sQuery(id+"F0.wireOp",EDGE,"E24.filletArc");Q0=makeQuery(id+"F2.boolean.opBoolean","SPLIT",FACE,{"disambiguationData":[TD([makeQuery(id+"F1.opExtrude","SWEPT_FACE",FACE,{"disambiguationData":[OSD([subQ5])]})])],"derivedFrom":makeQuery(id+"F1.opExtrude","CAP_FACE",FACE,{"disambiguationData":[OSD([subQ5,subQ7,subQ8,subQ9,subQ4,subQ3,subQ2,subQ1,subQ6,subQ0,subQ10,subQ11])],"isStart":true})});}
            var sketch = newSketch(context, id + "F16", { "sketchPlane" : qUnion([Q0])});
            skLineSegment(sketch, "E79", {"start": v(0, 74.25) * mm, "end": v(0, 104.25) * mm, "construction": true});
            skCircle(sketch, "E80", {"center": v(0, 104.25) * mm, "radius": 6 * mm});
            skLineSegment(sketch, "E81", {"start": v(-33, 74.25) * mm, "end": v(-15, 92.25) * mm});
            skLineSegment(sketch, "E82", {"start": v(-15, 92.25) * mm, "end": v(-15, 104.25) * mm});
            skLineSegment(sketch, "E83", {"start": v(33, 74.25) * mm, "end": v(15, 92.25) * mm});
            skLineSegment(sketch, "E84", {"start": v(15, 92.25) * mm, "end": v(15, 104.25) * mm});
            skArc(sketch, "E85", {"start": v(15, 104.25) * mm, "mid": v(0, 119.25) * mm, "end": v(-15, 104.25) * mm});
            skLineSegment(sketch, "E86", {"start": v(-74.25, 0) * mm, "end": v(74.25, 0) * mm, "construction": true});
            skCircle(sketch, "E87.MirrorC", {"center": v(0, -104.25) * mm, "radius": 6 * mm});
            skLineSegment(sketch, "E88.MirrorCS", {"start": v(15, -92.25) * mm, "end": v(15, -104.25) * mm});
            skLineSegment(sketch, "E89.MirrorCS", {"start": v(-15, -92.25) * mm, "end": v(-15, -104.25) * mm});
            skLineSegment(sketch, "E90.MirrorCS", {"start": v(0, -74.25) * mm, "end": v(0, -104.25) * mm, "construction": true});
            skLineSegment(sketch, "E91.MirrorCS", {"start": v(33, -74.25) * mm, "end": v(15, -92.25) * mm});
            skLineSegment(sketch, "E92.MirrorCS", {"start": v(-33, -74.25) * mm, "end": v(-15, -92.25) * mm});
            skArc(sketch, "E93.MirrorCS", {"start": v(15, -104.25) * mm, "mid": v(0, -119.25) * mm, "end": v(-15, -104.25) * mm});
            skSolve(sketch);
        }
        {
            var Q0;
            Q0=makeQuery(id+"F16.imprint","IMPRINT",FACE,{"disambiguationData":[TD([[makeQuery(id+"F16.imprint","IMPRINT",EDGE,{"derivedFrom":sQuery(id+"F16.wireOp",EDGE,"E80")}),-1.0]])]});
            var Q1;
            Q1=makeQuery(id+"F16.imprint","IMPRINT",FACE,{"disambiguationData":[TD([[makeQuery(id+"F16.imprint","IMPRINT",EDGE,{"derivedFrom":sQuery(id+"F16.wireOp",EDGE,"E87.MirrorC")}),1.0]])]});
            var Q2;
            Q2=makeQuery(id+"F16.imprint","IMPRINT",FACE,{"disambiguationData":[TD([[makeQuery(id+"F16.imprint","IMPRINT",EDGE,{"derivedFrom":makeQuery(id+"F1.opExtrude","CAP_EDGE",EDGE,{"disambiguationData":[OSD([sQuery(id+"F0.wireOp",EDGE,"E1.left")])],"isStart":true})}),-1.0]])]});
            var Q3;
            Q3=makeQuery(id+"F2.opExtrude","CAP_FACE",FACE,{"disambiguationData":[OSD([sQuery(id+"F0.wireOp",EDGE,"E12"),sQuery(id+"F0.wireOp",EDGE,"E13"),sQuery(id+"F0.wireOp",EDGE,"E14"),sQuery(id+"F0.wireOp",EDGE,"E15"),sQuery(id+"F0.wireOp",EDGE,"E17.filletArc"),sQuery(id+"F0.wireOp",EDGE,"E18.filletArc"),sQuery(id+"F0.wireOp",EDGE,"E19.filletArc"),sQuery(id+"F0.wireOp",EDGE,"E20.filletArc"),sQuery(id+"F0.wireOp",EDGE,"E25.0"),sQuery(id+"F0.wireOp",EDGE,"E25.1"),sQuery(id+"F0.wireOp",EDGE,"E25.2"),sQuery(id+"F0.wireOp",EDGE,"E25.3"),sQuery(id+"F0.wireOp",EDGE,"E25.4"),sQuery(id+"F0.wireOp",EDGE,"E25.5"),sQuery(id+"F0.wireOp",EDGE,"E25.6"),sQuery(id+"F0.wireOp",EDGE,"E25.7")])],"isStart":false});
            extrude(context, id + "F17", {"entities" : qUnion([Q0, Q1, Q2]), "operationType" : NewBodyOperationType.ADD, "endBound" : BoundingType.UP_TO_SURFACE, "endBoundEntityFace" : qUnion([Q3]), "depth" : 25 * mm});
        }
    });
